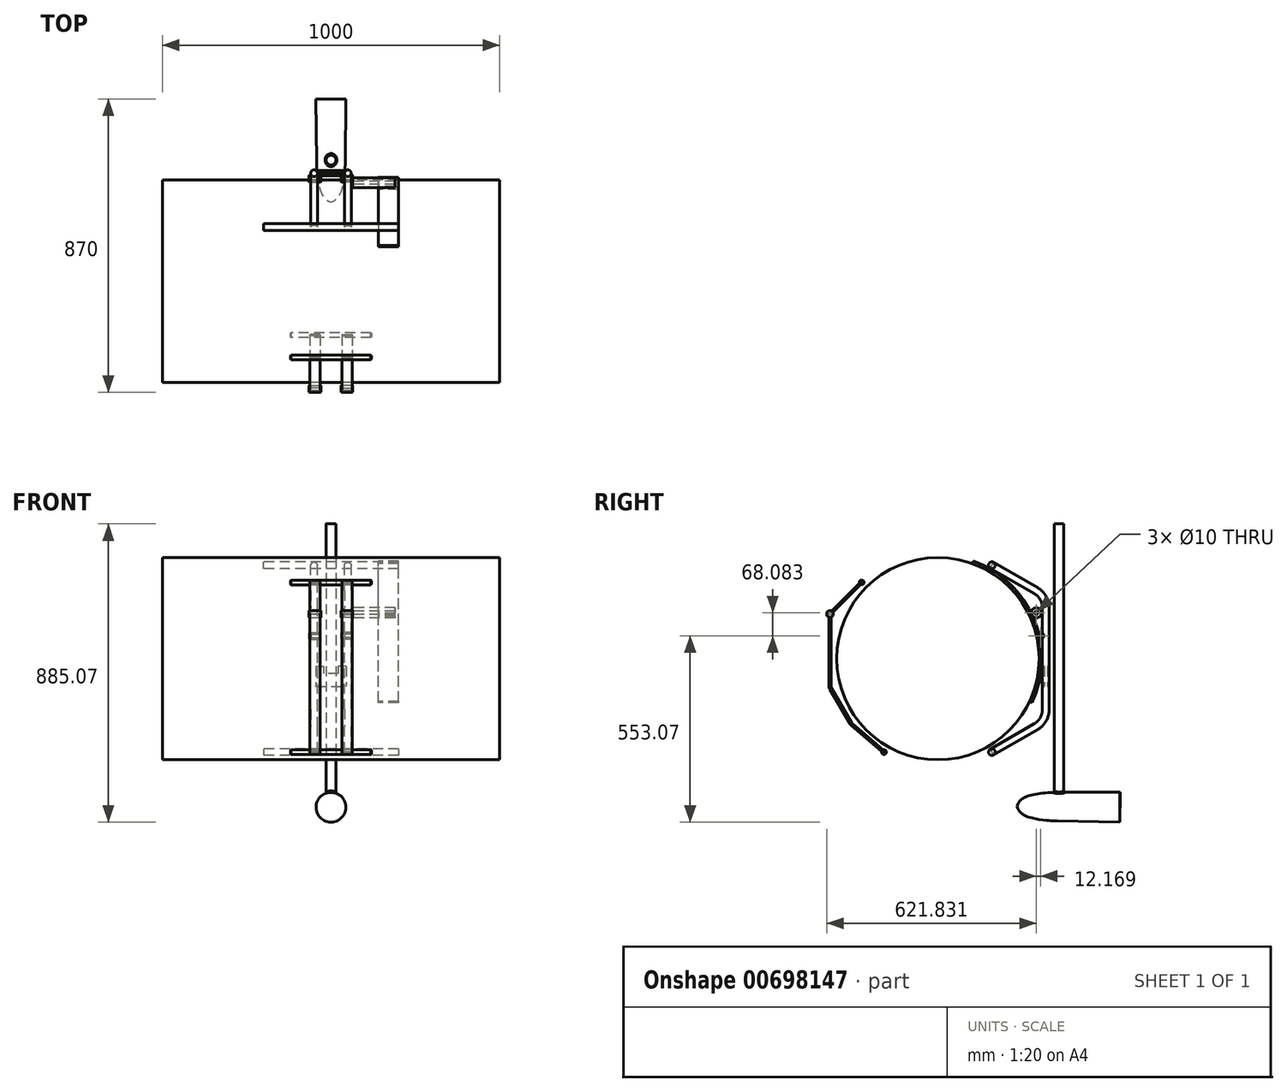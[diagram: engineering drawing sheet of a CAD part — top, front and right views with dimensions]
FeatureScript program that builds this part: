
annotation { "Feature Type Name" : "Feature", "Feature Type Description" : "" }
export const myFeature = defineFeature(function(context is Context, id is Id, definition is map)
    precondition{}
    {
        {
            var Q0;
            Q0=qCreatedBy(makeId("Right.planeOp"),FACE);
            var sketch = newSketch(context, id + "F0", { "sketchPlane" : qUnion([Q0])});
            skCircle(sketch, "E0", {"center": v(0, 0) * mm, "radius": 300 * mm});
            skCircle(sketch, "E1", {"center": v(0, 0) * mm, "radius": 320 * mm, "construction": true});
            skLineSegment(sketch, "E2", {"start": v(0, 0) * mm, "end": v(265.92, 460.59) * mm, "construction": true});
            skCircle(sketch, "E3", {"center": v(160, 277.13) * mm, "radius": 10 * mm});
            skSolve(sketch);
        }
        {
            var Q0;
            Q0=makeQuery(id+"F0.imprint","IMPRINT",FACE,{"disambiguationData":[TD([[makeQuery(id+"F0.imprint","IMPRINT",EDGE,{"derivedFrom":sQuery(id+"F0.wireOp",EDGE,"E0")}),1.0]])]});
            extrude(context, id + "F1", {"entities" : qUnion([Q0]), "endBound" : BoundingType.SYMMETRIC, "depth" : 1000 * mm, "offsetDistance" : 25 * mm});
        }
        {
            var Q0;
            Q0=makeQuery(id+"F0.imprint","IMPRINT",FACE,{"disambiguationData":[TD([[makeQuery(id+"F0.imprint","IMPRINT",EDGE,{"derivedFrom":sQuery(id+"F0.wireOp",EDGE,"E3")}),1.0]])]});
            extrude(context, id + "F2", {"entities" : qUnion([Q0]), "endBound" : BoundingType.SYMMETRIC, "depth" : 400 * mm, "offsetDistance" : 25 * mm});
        }
        {
            var Q0;
            Q0=makeQuery(id+"F2.opExtrude","SWEPT_BODY",BODY,{"disambiguationData":[OSD([sQuery(id+"F0.wireOp",EDGE,"E3")])]});
            var Q1;
            Q1=qCreatedBy(makeId("Top.planeOp"),FACE);
            mirror(context, id + "F3", {"entities" : qUnion([Q0]), "mirrorPlane" : qUnion([Q1])});
        }
        {
            var Q0;
            Q0=qCreatedBy(makeId("Right.planeOp"),FACE);
            var sketch = newSketch(context, id + "F4", { "sketchPlane" : qUnion([Q0])});
            skCircle(sketch, "E4", {"center": v(0, 0) * mm, "radius": 320 * mm, "construction": true});
            skLineSegment(sketch, "E5", {"start": v(160, 277.13) * mm, "end": v(290, 202.07) * mm});
            skLineSegment(sketch, "E6", {"start": v(320, 0) * mm, "end": v(320, 150.11) * mm});
            skPoint(sketch, "E7.visualSharp", {"position": v(320, 184.75) * mm});
            skArc(sketch, "E7.filletArc", {"start": v(320, 150.11) * mm, "mid": v(311.96, 180.11) * mm, "end": v(290, 202.07) * mm});
            skLineSegment(sketch, "E8.MirrorCS", {"start": v(160, -277.13) * mm, "end": v(290, -202.07) * mm});
            skArc(sketch, "E9.MirrorCS", {"start": v(320, -150.11) * mm, "mid": v(311.96, -180.11) * mm, "end": v(290, -202.07) * mm});
            skLineSegment(sketch, "E10.MirrorCS", {"start": v(320, 0) * mm, "end": v(320, -150.11) * mm});
            skSolve(sketch);
        }
        {
            var Q0;
            Q0=qCreatedBy(makeId("Top.planeOp"),FACE);
            var sketch = newSketch(context, id + "F5", { "sketchPlane" : qUnion([Q0])});
            skPoint(sketch, "E11.0", {"position": v(0, 320) * mm});
            skCircle(sketch, "E12", {"center": v(0, 320) * mm, "radius": 10 * mm});
            skSolve(sketch);
        }
        {
            var Q0;
            Q0=makeQuery(id+"F5.imprint","IMPRINT",FACE,{"disambiguationData":[TD([[makeQuery(id+"F5.imprint","IMPRINT",EDGE,{"derivedFrom":sQuery(id+"F5.wireOp",EDGE,"E12")}),1.0]])]});
            var Q1;
            Q1=sQuery(id+"F4.wireOp",EDGE,"E5");
            var Q2;
            Q2=sQuery(id+"F4.wireOp",EDGE,"E7.filletArc");
            var Q3;
            Q3=sQuery(id+"F4.wireOp",EDGE,"E6");
            var Q4;
            Q4=sQuery(id+"F4.wireOp",EDGE,"E10.MirrorCS");
            var Q5;
            Q5=sQuery(id+"F4.wireOp",EDGE,"E9.MirrorCS");
            var Q6;
            Q6=sQuery(id+"F4.wireOp",EDGE,"E8.MirrorCS");
            sweep(context, id + "F6", {"profiles" : qUnion([Q0]), "path" : qUnion([Q1, Q2, Q3, Q4, Q5, Q6])});
        }
        {
            var Q0;
            Q0=makeQuery(id+"F6.opSweep","SWEPT_BODY",BODY,{"disambiguationData":[OSD([sQuery(id+"F4.wireOp",EDGE,"E8.MirrorCS"),sQuery(id+"F5.wireOp",EDGE,"E12")])]});
            var Q1;
            Q1=makeQuery(id+"F2.opExtrude","SWEPT_FACE",FACE,{"disambiguationData":[OSD([sQuery(id+"F0.wireOp",EDGE,"E3")])]});
            transform(context, id + "F7", {"entities" : qUnion([Q0]), "transformType" : TransformType.TRANSLATION_DISTANCE, "transformDirection" : qUnion([Q1]), "distance" : 50 * mm, "makeCopy" : false});
        }
        {
            var Q0;
            Q0=makeQuery(id+"F6.opSweep","SWEPT_BODY",BODY,{"disambiguationData":[OSD([sQuery(id+"F4.wireOp",EDGE,"E8.MirrorCS"),sQuery(id+"F5.wireOp",EDGE,"E12")])]});
            var Q1;
            Q1=qCreatedBy(makeId("Right.planeOp"),FACE);
            mirror(context, id + "F8", {"entities" : qUnion([Q0]), "mirrorPlane" : qUnion([Q1])});
        }
        {
            var Q0;
            Q0=qCreatedBy(makeId("Front.planeOp"),FACE);
            cPlane(context, id + "F9", {"entities" : qUnion([Q0]), "cplaneType" : CPlaneType.OFFSET, "offset" : 320 * mm, "oppositeDirection" : true, "width" : 150 * mm, "height" : 150 * mm});
        }
        {
            var Q0;
            Q0=qCreatedBy(id+"F9.planeOp",FACE);
            var sketch = newSketch(context, id + "F10", { "sketchPlane" : qUnion([Q0])});
            skLineSegment(sketch, "E13", {"start": v(45, -22) * mm, "end": v(21.5, -22) * mm});
            skLineSegment(sketch, "E14", {"start": v(21.5, -22) * mm, "end": v(21.5, -44) * mm});
            skLineSegment(sketch, "E15", {"start": v(21.5, -44) * mm, "end": v(0, -44) * mm});
            skLineSegment(sketch, "E16", {"start": v(45, -22) * mm, "end": v(45, -82) * mm});
            skLineSegment(sketch, "E17", {"start": v(45, -82) * mm, "end": v(0, -82) * mm});
            skLineSegment(sketch, "E18.MirrorCS", {"start": v(-21.5, -44) * mm, "end": v(0, -44) * mm});
            skLineSegment(sketch, "E19.MirrorCS", {"start": v(-21.5, -22) * mm, "end": v(-21.5, -44) * mm});
            skLineSegment(sketch, "E20.MirrorCS", {"start": v(-45, -22) * mm, "end": v(-21.5, -22) * mm});
            skLineSegment(sketch, "E21.MirrorCS", {"start": v(-45, -22) * mm, "end": v(-45, -82) * mm});
            skLineSegment(sketch, "E22.MirrorCS", {"start": v(-45, -82) * mm, "end": v(0, -82) * mm});
            skSolve(sketch);
        }
        {
            var Q0;
            Q0 = qSketchRegion(id + "F10", true);
            extrude(context, id + "F11", {"entities" : qUnion([Q0]), "depth" : 7.5 * mm, "offsetDistance" : 25 * mm, "hasSecondDirection" : true, "secondDirectionOppositeDirection" : false, "secondDirectionDepth" : 4.5 * mm});
        }
        {
            var Q0;
            Q0=makeQuery(id+"F11.opExtrude","CAP_EDGE",EDGE,{"disambiguationData":[OSD([sQuery(id+"F10.wireOp",EDGE,"E13")])],"isStart":true});
            var Q1;
            Q1=makeQuery(id+"F11.opExtrude","CAP_EDGE",EDGE,{"disambiguationData":[OSD([sQuery(id+"F10.wireOp",EDGE,"E13")])],"isStart":false});
            var Q2;
            Q2=makeQuery(id+"F11.opExtrude","CAP_EDGE",EDGE,{"disambiguationData":[OSD([sQuery(id+"F10.wireOp",EDGE,"E20.MirrorCS")])],"isStart":true});
            var Q3;
            Q3=makeQuery(id+"F11.opExtrude","CAP_EDGE",EDGE,{"disambiguationData":[OSD([sQuery(id+"F10.wireOp",EDGE,"E20.MirrorCS")])],"isStart":false});
            var Q4;
            Q4=makeQuery(id+"F11.opExtrude","CAP_EDGE",EDGE,{"disambiguationData":[OSD([sQuery(id+"F10.wireOp",EDGE,"E17"),sQuery(id+"F10.wireOp",EDGE,"E22.MirrorCS")])],"isStart":true});
            var Q5;
            Q5=makeQuery(id+"F11.opExtrude","CAP_EDGE",EDGE,{"disambiguationData":[OSD([sQuery(id+"F10.wireOp",EDGE,"E17"),sQuery(id+"F10.wireOp",EDGE,"E22.MirrorCS")])],"isStart":false});
            fillet(context, id + "F12", {"entities" : qUnion([Q0, Q1, Q2, Q3, Q4, Q5]), "radius" : 1 * mm, "tangentPropagation" : true, "allowEdgeOverflow" : false});
        }
        {
            var Q0;
            Q0=qCreatedBy(makeId("Right.planeOp"),FACE);
            var sketch = newSketch(context, id + "F13", { "sketchPlane" : qUnion([Q0])});
            skLineSegment(sketch, "E23", {"start": v(0, 0) * mm, "end": v(385.54, 0) * mm, "construction": true});
            skCircle(sketch, "E24", {"center": v(304, 68) * mm, "radius": 10 * mm});
            skCircle(sketch, "E25", {"center": v(304, 68) * mm, "radius": 5 * mm});
            skSolve(sketch);
        }
        {
            var Q0;
            Q0 = qSketchRegion(id + "F13", true);
            extrude(context, id + "F14", {"entities" : qUnion([Q0]), "depth" : 35 * mm, "offsetDistance" : 25 * mm});
        }
        {
            var Q0;
            Q0=makeQuery(id+"F14.opExtrude","SWEPT_BODY",BODY,{"disambiguationData":[OSD([sQuery(id+"F13.wireOp",EDGE,"E24"),sQuery(id+"F13.wireOp",EDGE,"E25")])]});
            var Q1;
            Q1=makeQuery(id+"F2.opExtrude","SWEPT_FACE",FACE,{"disambiguationData":[OSD([sQuery(id+"F0.wireOp",EDGE,"E3")])]});
            transform(context, id + "F15", {"entities" : qUnion([Q0]), "transformType" : TransformType.TRANSLATION_DISTANCE, "transformDirection" : qUnion([Q1]), "distance" : 30 * mm, "oppositeDirection" : true, "makeCopy" : false});
        }
        {
            var Q0;
            Q0=makeQuery(id+"F14.opExtrude","CAP_EDGE",EDGE,{"disambiguationData":[OSD([sQuery(id+"F13.wireOp",EDGE,"E24")])],"isStart":false});
            var Q1;
            Q1=makeQuery(id+"F14.opExtrude","CAP_EDGE",EDGE,{"disambiguationData":[OSD([sQuery(id+"F13.wireOp",EDGE,"E25")])],"isStart":false});
            var Q2;
            Q2=makeQuery(id+"F14.opExtrude","CAP_EDGE",EDGE,{"disambiguationData":[OSD([sQuery(id+"F13.wireOp",EDGE,"E24")])],"isStart":true});
            var Q3;
            Q3=makeQuery(id+"F14.opExtrude","CAP_EDGE",EDGE,{"disambiguationData":[OSD([sQuery(id+"F13.wireOp",EDGE,"E25")])],"isStart":true});
            chamfer(context, id + "F16", {"entities" : qUnion([Q0, Q1, Q2, Q3]), "width" : 1 * mm, "tangentPropagation" : true});
        }
        {
            var Q0;
            Q0=makeQuery(id+"F14.opExtrude","SWEPT_BODY",BODY,{"disambiguationData":[OSD([sQuery(id+"F13.wireOp",EDGE,"E24"),sQuery(id+"F13.wireOp",EDGE,"E25")])]});
            var Q1;
            Q1=qCreatedBy(makeId("Right.planeOp"),FACE);
            mirror(context, id + "F17", {"operationType" : NewBodyOperationType.ADD, "entities" : qUnion([Q0]), "mirrorPlane" : qUnion([Q1])});
        }
        {
            var Q0;
            Q0=qCreatedBy(makeId("Top.planeOp"),FACE);
            var sketch = newSketch(context, id + "F18", { "sketchPlane" : qUnion([Q0])});
            skLineSegment(sketch, "E26", {"start": v(0, 0) * mm, "end": v(0, 431.37) * mm, "construction": true});
            skCircle(sketch, "E27", {"center": v(0, 359) * mm, "radius": 14.5 * mm});
            skSolve(sketch);
        }
        {
            var Q0;
            Q0=makeQuery(id+"F18.imprint","IMPRINT",FACE,{"disambiguationData":[TD([[makeQuery(id+"F18.imprint","IMPRINT",EDGE,{"derivedFrom":sQuery(id+"F18.wireOp",EDGE,"E27")}),1.0]])]});
            extrude(context, id + "F19", {"entities" : qUnion([Q0]), "endBound" : BoundingType.SYMMETRIC, "depth" : 800 * mm, "offsetDistance" : 25 * mm});
        }
        {
            var Q0;
            Q0=makeQuery(id+"F11.opExtrude","SWEPT_BODY",BODY,{"disambiguationData":[OSD([sQuery(id+"F10.wireOp",EDGE,"E13"),sQuery(id+"F10.wireOp",EDGE,"E14"),sQuery(id+"F10.wireOp",EDGE,"E15"),sQuery(id+"F10.wireOp",EDGE,"E16"),sQuery(id+"F10.wireOp",EDGE,"E17"),sQuery(id+"F10.wireOp",EDGE,"E18.MirrorCS"),sQuery(id+"F10.wireOp",EDGE,"E19.MirrorCS"),sQuery(id+"F10.wireOp",EDGE,"E20.MirrorCS"),sQuery(id+"F10.wireOp",EDGE,"E21.MirrorCS"),sQuery(id+"F10.wireOp",EDGE,"E22.MirrorCS")])]});
            var Q1;
            Q1=qCreatedBy(id+"F9.planeOp",FACE);
            mirror(context, id + "F20", {"entities" : qUnion([Q0]), "mirrorPlane" : qUnion([Q1])});
        }
        {
            var Q0;
            Q0=qCreatedBy(makeId("Right.planeOp"),FACE);
            var sketch = newSketch(context, id + "F21", { "sketchPlane" : qUnion([Q0])});
            skLineSegment(sketch, "E28", {"start": v(8.12, -438) * mm, "end": v(538.87, -438) * mm, "construction": true});
            skLineSegment(sketch, "E29", {"start": v(235, -396.5) * mm, "end": v(384.53, -396.5) * mm, "construction": true});
            skLineSegment(sketch, "E30", {"start": v(355, -389.88) * mm, "end": v(355, -511.75) * mm, "construction": true});
            skFitSpline(sketch, "E31", {"points": [v(355, -396.5) * mm, v(273.73, -405.4) * mm, v(244.54, -420.82) * mm, v(235.02, -438) * mm], "startDerivative": vector(-142.28, 0) * mm, "endDerivative": vector(-0.8, -75.3) * mm});
            skLineSegment(sketch, "E32", {"start": v(355, -396.5) * mm, "end": v(540, -396.5) * mm});
            skLineSegment(sketch, "E33", {"start": v(540, -396.5) * mm, "end": v(540, -440.8) * mm});
            skLineSegment(sketch, "E34", {"start": v(235.02, -438) * mm, "end": v(540, -440.8) * mm});
            skSolve(sketch);
        }
        {
            var Q0;
            Q0 = qSketchRegion(id + "F21", true);
            var Q1;
            Q1=sQuery(id+"F21.wireOp",EDGE,"E34");
            revolve(context, id + "F22", {"entities" : qUnion([Q0]), "axis" : qUnion([Q1]), "revolveType" : RevolveType.FULL});
        }
        {
            var Q0;
            Q0=sQuery(id+"F0.wireOp",EDGE,"E0");
            extrude(context, id + "F23", {"bodyType" : ToolBodyType.SURFACE, "surfaceEntities" : qUnion([Q0]), "endBound" : BoundingType.SYMMETRIC, "depth" : 1000 * mm, "offsetDistance" : 25 * mm});
        }
        {
            var Q0;
            Q0=makeQuery(id+"F19.opExtrude","SWEPT_BODY",BODY,{"disambiguationData":[OSD([sQuery(id+"F18.wireOp",EDGE,"E27")])]});
            var Q1;
            Q1=makeQuery(id+"F22.opRevolve","SWEPT_BODY",BODY,{"disambiguationData":[OSD([sQuery(id+"F21.wireOp",EDGE,"E31"),sQuery(id+"F21.wireOp",EDGE,"E32"),sQuery(id+"F21.wireOp",EDGE,"E33"),sQuery(id+"F21.wireOp",EDGE,"E34")])]});
            booleanBodies(context, id + "F24", {"operationType" : BooleanOperationType.UNION, "tools" : qUnion([Q0, Q1])});
        }
        {
            var Q0;
            Q0=makeQuery(id+"F24.opBoolean","INTERSECT",EDGE,{"derivedFrom":[makeQuery(id+"F19.opExtrude","SWEPT_FACE",FACE,{"disambiguationData":[OSD([sQuery(id+"F18.wireOp",EDGE,"E27")])]}),makeQuery(id+"F22.opRevolve","SWEPT_FACE",FACE,{"disambiguationData":[OSD([sQuery(id+"F21.wireOp",EDGE,"E32")])]})]});
            fillet(context, id + "F25", {"entities" : qUnion([Q0]), "radius" : 5 * mm, "tangentPropagation" : true, "allowEdgeOverflow" : false});
        }
        {
            var Q0;
            Q0=qCreatedBy(makeId("Right.planeOp"),FACE);
            var sketch = newSketch(context, id + "F26", { "sketchPlane" : qUnion([Q0])});
            skLineSegment(sketch, "E35", {"start": v(0, 0) * mm, "end": v(-299.7, 299.7) * mm, "construction": true});
            skCircle(sketch, "E36", {"center": v(0, 0) * mm, "radius": 320 * mm, "construction": true});
            skLineSegment(sketch, "E37", {"start": v(0, 0) * mm, "end": v(-183.94, -318.59) * mm, "construction": true});
            skCircle(sketch, "E38", {"center": v(-226.27, 226.27) * mm, "radius": 7 * mm});
            skCircle(sketch, "E39", {"center": v(-160, -277.13) * mm, "radius": 7 * mm});
            skLineSegment(sketch, "E40", {"start": v(-320, 0) * mm, "end": v(-320, 287.4) * mm, "construction": true});
            skLineSegment(sketch, "E41", {"start": v(-226.27, 226.27) * mm, "end": v(-320, 132.55) * mm, "construction": true});
            skSolve(sketch);
        }
        {
            var Q0;
            Q0 = qSketchRegion(id + "F26", true);
            extrude(context, id + "F27", {"entities" : qUnion([Q0]), "endBound" : BoundingType.SYMMETRIC, "depth" : 240 * mm, "offsetDistance" : 25 * mm});
        }
        {
            var Q0;
            Q0=qCreatedBy(makeId("Right.planeOp"),FACE);
            var sketch = newSketch(context, id + "F28", { "sketchPlane" : qUnion([Q0])});
            skPoint(sketch, "E42.0", {"position": v(-320, 132.55) * mm});
            skCircle(sketch, "E43", {"center": v(-320, 132.55) * mm, "radius": 10 * mm});
            skSolve(sketch);
        }
        {
            var Q0;
            Q0=makeQuery(id+"F28.imprint","IMPRINT",FACE,{"disambiguationData":[TD([[makeQuery(id+"F28.imprint","IMPRINT",EDGE,{"derivedFrom":sQuery(id+"F28.wireOp",EDGE,"7lmwxcnG-TXEm-FUzH-tSau-3Nbo2HM707GO")}),-1.0]])]});
            var Q1;
            Q1=makeQuery(id+"F28.imprint","IMPRINT",FACE,{"disambiguationData":[TD([[makeQuery(id+"F28.imprint","IMPRINT",EDGE,{"derivedFrom":sQuery(id+"F28.wireOp",EDGE,"E43")}),1.0]])]});
            extrude(context, id + "F29", {"entities" : qUnion([Q0, Q1]), "depth" : 65 * mm, "offsetDistance" : 25 * mm, "hasSecondDirection" : true, "secondDirectionOppositeDirection" : false, "secondDirectionDepth" : 30 * mm});
        }
        {
            var Q0;
            Q0=qCreatedBy(makeId("Right.planeOp"),FACE);
            cPlane(context, id + "F30", {"entities" : qUnion([Q0]), "cplaneType" : CPlaneType.OFFSET, "offset" : 47.5 * mm, "width" : 150 * mm, "height" : 150 * mm});
        }
        {
            var Q0;
            Q0=qCreatedBy(id+"F30.planeOp",FACE);
            var sketch = newSketch(context, id + "F31", { "sketchPlane" : qUnion([Q0])});
            skLineSegment(sketch, "E44.0", {"start": v(-226.27, 226.27) * mm, "end": v(-320, 132.55) * mm});
            skPoint(sketch, "E45.orphan", {"position": v(-320, 287.4) * mm});
            skPoint(sketch, "E46.0", {"position": v(-160, -277.13) * mm});
            skPoint(sketch, "E47.orphan", {"position": v(-320, 0) * mm});
            skLineSegment(sketch, "E48", {"start": v(0, 0) * mm, "end": v(-298.19, -224.7) * mm, "construction": true});
            skLineSegment(sketch, "E49", {"start": v(-320, 132.55) * mm, "end": v(-320, -81.72) * mm});
            skLineSegment(sketch, "E50", {"start": v(0, 0) * mm, "end": v(-331.42, -191.34) * mm, "construction": true});
            skLineSegment(sketch, "E51", {"start": v(-318, -89.22) * mm, "end": v(-258.77, -191.79) * mm});
            skLineSegment(sketch, "E52", {"start": v(-160, -277.13) * mm, "end": v(-255.52, -195.7) * mm});
            skPoint(sketch, "E53.visualSharp", {"position": v(-257.48, -194.03) * mm});
            skArc(sketch, "E53.filletArc", {"start": v(-258.77, -191.79) * mm, "mid": v(-257.31, -193.89) * mm, "end": v(-255.52, -195.7) * mm});
            skPoint(sketch, "E54.visualSharp", {"position": v(-320, -85.74) * mm});
            skArc(sketch, "E54.filletArc", {"start": v(-320, -81.72) * mm, "mid": v(-319.49, -85.6) * mm, "end": v(-318, -89.22) * mm});
            skSolve(sketch);
        }
        {
            var Q0;
            Q0=qCreatedBy(makeId("Top.planeOp"),FACE);
            var sketch = newSketch(context, id + "F32", { "sketchPlane" : qUnion([Q0])});
            skLineSegment(sketch, "E55.bottom", {"start": v(32.5, -317) * mm, "end": v(62.5, -317) * mm});
            skLineSegment(sketch, "E55.top", {"start": v(32.5, -323) * mm, "end": v(62.5, -323) * mm});
            skLineSegment(sketch, "E55.left", {"start": v(32.5, -317) * mm, "end": v(32.5, -323) * mm});
            skLineSegment(sketch, "E55.right", {"start": v(62.5, -317) * mm, "end": v(62.5, -323) * mm});
            skSolve(sketch);
        }
        {
            var Q0;
            Q0=makeQuery(id+"F32.imprint","IMPRINT",FACE,{"disambiguationData":[TD([[makeQuery(id+"F32.imprint","IMPRINT",EDGE,{"derivedFrom":sQuery(id+"F32.wireOp",EDGE,"E55.bottom")}),-1.0]])]});
            var Q1;
            Q1=sQuery(id+"F31.wireOp",EDGE,"E44.0");
            var Q2;
            Q2=sQuery(id+"F31.wireOp",EDGE,"E49");
            var Q3;
            Q3=sQuery(id+"F31.wireOp",EDGE,"E54.filletArc");
            var Q4;
            Q4=sQuery(id+"F31.wireOp",EDGE,"E51");
            var Q5;
            Q5=sQuery(id+"F31.wireOp",EDGE,"E53.filletArc");
            var Q6;
            Q6=sQuery(id+"F31.wireOp",EDGE,"E52");
            sweep(context, id + "F33", {"profiles" : qUnion([Q0]), "path" : qUnion([Q1, Q2, Q3, Q4, Q5, Q6])});
        }
        {
            var Q0;
            Q0=makeQuery(id+"F33.opSweep","SWEPT_EDGE",EDGE,{"disambiguationData":[OSD([sQuery(id+"F31.wireOp",EDGE,"E49"),sQuery(id+"F32.wireOp",EDGE,"E55.bottom"),sQuery(id+"F32.wireOp",EDGE,"E55.right")])]});
            var Q1;
            Q1=makeQuery(id+"F33.opSweep","SWEPT_EDGE",EDGE,{"disambiguationData":[OSD([sQuery(id+"F31.wireOp",EDGE,"E49"),sQuery(id+"F32.wireOp",EDGE,"E55.top"),sQuery(id+"F32.wireOp",EDGE,"E55.left")])]});
            var Q2;
            Q2=makeQuery(id+"F33.opSweep","SWEPT_EDGE",EDGE,{"disambiguationData":[OSD([sQuery(id+"F31.wireOp",EDGE,"E49"),sQuery(id+"F32.wireOp",EDGE,"E55.bottom"),sQuery(id+"F32.wireOp",EDGE,"E55.left")])]});
            var Q3;
            Q3=makeQuery(id+"F33.opSweep","SWEPT_EDGE",EDGE,{"disambiguationData":[OSD([sQuery(id+"F31.wireOp",EDGE,"E49"),sQuery(id+"F32.wireOp",EDGE,"E55.top"),sQuery(id+"F32.wireOp",EDGE,"E55.right")])]});
            var Q4;
            Q4=makeQuery(id+"F33.opSweep","SWEPT_EDGE",EDGE,{"disambiguationData":[OSD([sQuery(id+"F31.wireOp",EDGE,"E44.0"),sQuery(id+"F32.wireOp",EDGE,"E55.top"),sQuery(id+"F32.wireOp",EDGE,"E55.right")])]});
            var Q5;
            Q5=makeQuery(id+"F33.opSweep","SWEPT_EDGE",EDGE,{"disambiguationData":[OSD([sQuery(id+"F31.wireOp",EDGE,"E44.0"),sQuery(id+"F32.wireOp",EDGE,"E55.bottom"),sQuery(id+"F32.wireOp",EDGE,"E55.right")])]});
            var Q6;
            Q6=makeQuery(id+"F33.opSweep","SWEPT_EDGE",EDGE,{"disambiguationData":[OSD([sQuery(id+"F31.wireOp",EDGE,"E44.0"),sQuery(id+"F32.wireOp",EDGE,"E55.top"),sQuery(id+"F32.wireOp",EDGE,"E55.left")])]});
            var Q7;
            Q7=makeQuery(id+"F33.opSweep","SWEPT_EDGE",EDGE,{"disambiguationData":[OSD([sQuery(id+"F31.wireOp",EDGE,"E44.0"),sQuery(id+"F32.wireOp",EDGE,"E55.bottom"),sQuery(id+"F32.wireOp",EDGE,"E55.left")])]});
            fillet(context, id + "F34", {"entities" : qUnion([Q0, Q1, Q2, Q3, Q4, Q5, Q6, Q7]), "radius" : 1 * mm, "tangentPropagation" : true, "allowEdgeOverflow" : false});
        }
        {
            var Q0;
            Q0=makeQuery(id+"F33.opSweep","SWEPT_BODY",BODY,{"disambiguationData":[OSD([sQuery(id+"F31.wireOp",EDGE,"E52"),sQuery(id+"F32.wireOp",EDGE,"E55.bottom"),sQuery(id+"F32.wireOp",EDGE,"E55.top"),sQuery(id+"F32.wireOp",EDGE,"E55.left"),sQuery(id+"F32.wireOp",EDGE,"E55.right")])]});
            var Q1;
            Q1=makeQuery(id+"F29.opExtrude","SWEPT_BODY",BODY,{"disambiguationData":[OSD([sQuery(id+"F28.wireOp",EDGE,"7lmwxcnG-TXEm-FUzH-tSau-3Nbo2HM707GO"),sQuery(id+"F28.wireOp",EDGE,"E43")])]});
            var Q2;
            Q2=qCreatedBy(makeId("Right.planeOp"),FACE);
            mirror(context, id + "F35", {"entities" : qUnion([Q0, Q1]), "mirrorPlane" : qUnion([Q2])});
        }
        {
            var Q0;
            Q0=sQuery(id+"F28.wireOp",VERTEX,"E42.0");
            var Q1;
            Q1=makeQuery(id+"F27.opExtrude","SWEPT_BODY",BODY,{"disambiguationData":[OSD([sQuery(id+"F26.wireOp",EDGE,"E38")])]});
            hole(context, id + "F36", {"style" : HoleStyle.SIMPLE, "endStyle" : HoleEndStyle.THROUGH, "oppositeDirection" : true, "holeDiameter" : 10 * mm, "majorDiameter" : 5 * mm, "isTappedThrough" : true, "tappedDepth" : 12 * mm, "tapClearance" : 3, "locations" : qUnion([Q0]), "scope" : qUnion([Q1])});
        }
        {
            var Q0;
            Q0=sQuery(id+"F28.wireOp",VERTEX,"E42.0");
            var Q1;
            Q1=makeQuery(id+"F27.opExtrude","SWEPT_BODY",BODY,{"disambiguationData":[OSD([sQuery(id+"F26.wireOp",EDGE,"E38")])]});
            hole(context, id + "F37", {"style" : HoleStyle.SIMPLE, "endStyle" : HoleEndStyle.THROUGH, "holeDiameter" : 10 * mm, "majorDiameter" : 5 * mm, "isTappedThrough" : true, "tappedDepth" : 12 * mm, "tapClearance" : 3, "locations" : qUnion([Q0]), "scope" : qUnion([Q1])});
        }
        {
            var Q0;
            Q0=makeQuery(id+"F27.opExtrude","CAP_EDGE",EDGE,{"disambiguationData":[OSD([sQuery(id+"F26.wireOp",EDGE,"E38")])],"isStart":true});
            var Q1;
            Q1=makeQuery(id+"F27.opExtrude","CAP_EDGE",EDGE,{"disambiguationData":[OSD([sQuery(id+"F26.wireOp",EDGE,"E38")])],"isStart":false});
            var Q2;
            Q2=makeQuery(id+"F27.opExtrude","CAP_EDGE",EDGE,{"disambiguationData":[OSD([sQuery(id+"F26.wireOp",EDGE,"E39")])],"isStart":true});
            var Q3;
            Q3=makeQuery(id+"F27.opExtrude","CAP_EDGE",EDGE,{"disambiguationData":[OSD([sQuery(id+"F26.wireOp",EDGE,"E39")])],"isStart":false});
            chamfer(context, id + "F38", {"entities" : qUnion([Q0, Q1, Q2, Q3]), "width" : 2 * mm, "tangentPropagation" : true});
        }
        {
            var Q0;
            Q0=qCreatedBy(makeId("Right.planeOp"),FACE);
            cPlane(context, id + "F39", {"entities" : qUnion([Q0]), "cplaneType" : CPlaneType.OFFSET, "offset" : 170 * mm, "width" : 150 * mm, "height" : 150 * mm});
        }
        {
            var Q0;
            Q0=qCreatedBy(id+"F39.planeOp",FACE);
            var sketch = newSketch(context, id + "F40", { "sketchPlane" : qUnion([Q0])});
            skArc(sketch, "E56", {"start": v(105.34, 289.43) * mm, "mid": v(284.55, 117.87) * mm, "end": v(279.14, -130.17) * mm});
            skLineSegment(sketch, "E57", {"start": v(0, 0) * mm, "end": v(105.34, 289.43) * mm, "construction": true});
            skLineSegment(sketch, "E58", {"start": v(0, 0) * mm, "end": v(279.14, -130.17) * mm, "construction": true});
            skArc(sketch, "E59", {"start": v(102.6, 281.9) * mm, "mid": v(277.16, 114.8) * mm, "end": v(271.9, -126.79) * mm});
            skLineSegment(sketch, "E60", {"start": v(102.6, 281.9) * mm, "end": v(105.34, 289.43) * mm});
            skLineSegment(sketch, "E61", {"start": v(271.9, -126.79) * mm, "end": v(279.14, -130.17) * mm});
            skSolve(sketch);
        }
        {
            var Q0;
            Q0=qCreatedBy(id+"F39.planeOp",FACE);
            var sketch = newSketch(context, id + "F41", { "sketchPlane" : qUnion([Q0])});
            skLineSegment(sketch, "E62", {"start": v(0, 0) * mm, "end": v(291.83, 136.08) * mm, "construction": true});
            skCircle(sketch, "E63", {"center": v(291.83, 136.08) * mm, "radius": 15 * mm});
            skCircle(sketch, "E64", {"center": v(291.83, 136.08) * mm, "radius": 5 * mm});
            skSolve(sketch);
        }
        {
            var Q0;
            Q0 = qSketchRegion(id + "F40", true);
            extrude(context, id + "F42", {"entities" : qUnion([Q0]), "endBound" : BoundingType.SYMMETRIC, "depth" : 60 * mm, "offsetDistance" : 25 * mm});
        }
        {
            var Q0;
            Q0 = qSketchRegion(id + "F41", true);
            extrude(context, id + "F43", {"entities" : qUnion([Q0]), "operationType" : NewBodyOperationType.ADD, "depth" : 20 * mm, "offsetDistance" : 25 * mm, "hasSecondDirection" : true, "secondDirectionOppositeDirection" : true, "secondDirectionDepth" : 105 * mm});
        }
    });
